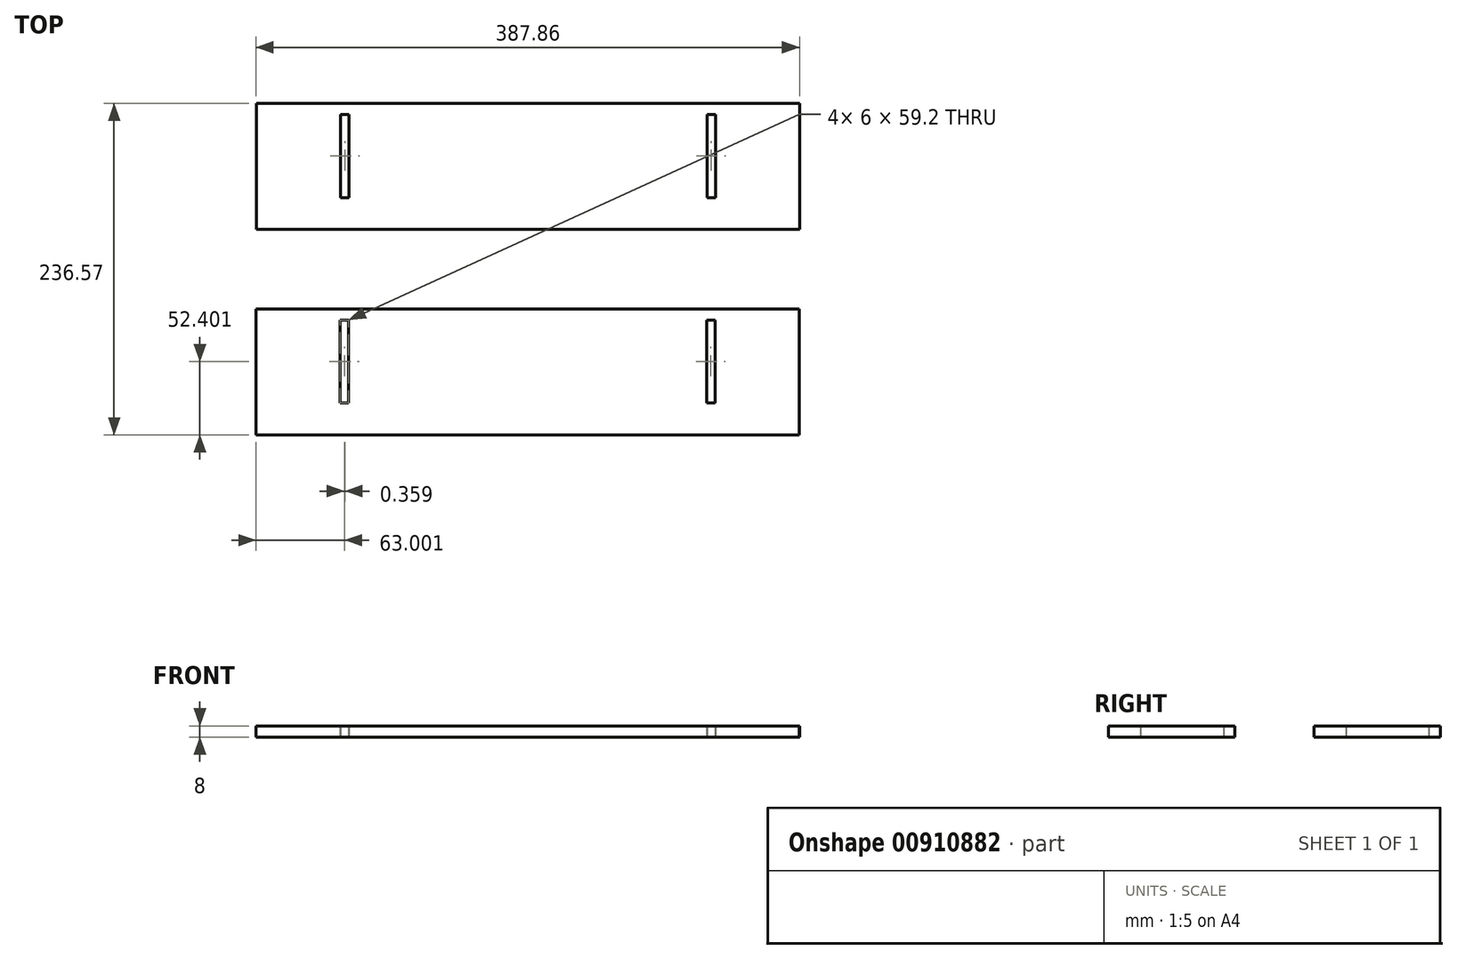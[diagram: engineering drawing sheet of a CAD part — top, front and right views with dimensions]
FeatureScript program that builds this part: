
annotation { "Feature Type Name" : "Feature", "Feature Type Description" : "" }
export const myFeature = defineFeature(function(context is Context, id is Id, definition is map)
    precondition{}
    {
        {
            var Q0;
            Q0=qCreatedBy(makeId("Top.planeOp"),FACE);
            var sketch = newSketch(context, id + "F0", { "sketchPlane" : qUnion([Q0])});
            skLineSegment(sketch, "E0", {"start": v(-35.86, 49.24) * mm, "end": v(-35.86, -40.76) * mm});
            skLineSegment(sketch, "E1", {"start": v(-35.86, 49.24) * mm, "end": v(351.64, 49.24) * mm});
            skLineSegment(sketch, "E2", {"start": v(-35.86, -40.76) * mm, "end": v(351.64, -40.76) * mm});
            skLineSegment(sketch, "E3", {"start": v(351.64, -40.76) * mm, "end": v(351.64, 49.24) * mm});
            skLineSegment(sketch, "E4", {"start": v(-43.04, 41.24) * mm, "end": v(357.86, 41.24) * mm, "construction": true});
            skLineSegment(sketch, "E5", {"start": v(-42.33, -17.96) * mm, "end": v(359.17, -17.96) * mm, "construction": true});
            skLineSegment(sketch, "E6", {"start": v(24.14, 67.8) * mm, "end": v(24.14, -60.96) * mm, "construction": true});
            skLineSegment(sketch, "E7", {"start": v(291.64, 73.52) * mm, "end": v(291.64, -68.64) * mm, "construction": true});
            skLineSegment(sketch, "E8.bottom", {"start": v(24.14, 41.24) * mm, "end": v(30.14, 41.24) * mm});
            skLineSegment(sketch, "E8.top", {"start": v(24.14, -17.96) * mm, "end": v(30.14, -17.96) * mm});
            skLineSegment(sketch, "E8.left", {"start": v(24.14, 41.24) * mm, "end": v(24.14, -17.96) * mm});
            skLineSegment(sketch, "E8.right", {"start": v(30.14, 41.24) * mm, "end": v(30.14, -17.96) * mm});
            skLineSegment(sketch, "E9.bottom", {"start": v(291.64, 41.24) * mm, "end": v(285.64, 41.24) * mm});
            skLineSegment(sketch, "E9.top", {"start": v(291.64, -17.96) * mm, "end": v(285.64, -17.96) * mm});
            skLineSegment(sketch, "E9.left", {"start": v(291.64, 41.24) * mm, "end": v(291.64, -17.96) * mm});
            skLineSegment(sketch, "E9.right", {"start": v(285.64, 41.24) * mm, "end": v(285.64, -17.96) * mm});
            skLineSegment(sketch, "E10", {"start": v(-36.22, -97.33) * mm, "end": v(-36.22, -187.33) * mm});
            skLineSegment(sketch, "E11", {"start": v(-36.22, -97.33) * mm, "end": v(351.28, -97.33) * mm});
            skLineSegment(sketch, "E12", {"start": v(-36.22, -187.33) * mm, "end": v(351.28, -187.33) * mm});
            skLineSegment(sketch, "E13", {"start": v(351.28, -187.33) * mm, "end": v(351.28, -97.33) * mm});
            skLineSegment(sketch, "E14", {"start": v(-48.28, -105.33) * mm, "end": v(352.62, -105.33) * mm, "construction": true});
            skLineSegment(sketch, "E15", {"start": v(-47.56, -164.53) * mm, "end": v(353.93, -164.53) * mm, "construction": true});
            skLineSegment(sketch, "E16", {"start": v(23.78, -77.2) * mm, "end": v(23.78, -205.96) * mm, "construction": true});
            skLineSegment(sketch, "E17", {"start": v(291.28, -81.6) * mm, "end": v(291.28, -219.4) * mm, "construction": true});
            skLineSegment(sketch, "E18.bottom", {"start": v(23.78, -105.33) * mm, "end": v(29.78, -105.33) * mm});
            skLineSegment(sketch, "E18.top", {"start": v(23.78, -164.53) * mm, "end": v(29.78, -164.53) * mm});
            skLineSegment(sketch, "E18.left", {"start": v(23.78, -105.33) * mm, "end": v(23.78, -164.53) * mm});
            skLineSegment(sketch, "E18.right", {"start": v(29.78, -105.33) * mm, "end": v(29.78, -164.53) * mm});
            skLineSegment(sketch, "E19.bottom", {"start": v(291.28, -105.33) * mm, "end": v(285.28, -105.33) * mm});
            skLineSegment(sketch, "E19.top", {"start": v(291.28, -164.53) * mm, "end": v(285.28, -164.53) * mm});
            skLineSegment(sketch, "E19.left", {"start": v(291.28, -105.33) * mm, "end": v(291.28, -164.53) * mm});
            skLineSegment(sketch, "E19.right", {"start": v(285.28, -105.33) * mm, "end": v(285.28, -164.53) * mm});
            skSolve(sketch);
        }
        {
            var Q0;
            Q0=makeQuery(id+"F0.imprint","IMPRINT",FACE,{"disambiguationData":[TD([[makeQuery(id+"F0.imprint","IMPRINT",EDGE,{"derivedFrom":sQuery(id+"F0.wireOp",EDGE,"E0")}),1.0]])]});
            extrude(context, id + "F1", {"entities" : qUnion([Q0]), "depth" : 8 * mm, "offsetDistance" : 25 * mm});
        }
        {
            var Q0;
            Q0=makeQuery(id+"F0.imprint","IMPRINT",FACE,{"disambiguationData":[TD([[makeQuery(id+"F0.imprint","IMPRINT",EDGE,{"derivedFrom":sQuery(id+"F0.wireOp",EDGE,"E10")}),1.0]])]});
            extrude(context, id + "F2", {"entities" : qUnion([Q0]), "depth" : 8 * mm, "offsetDistance" : 25 * mm});
        }
    });
